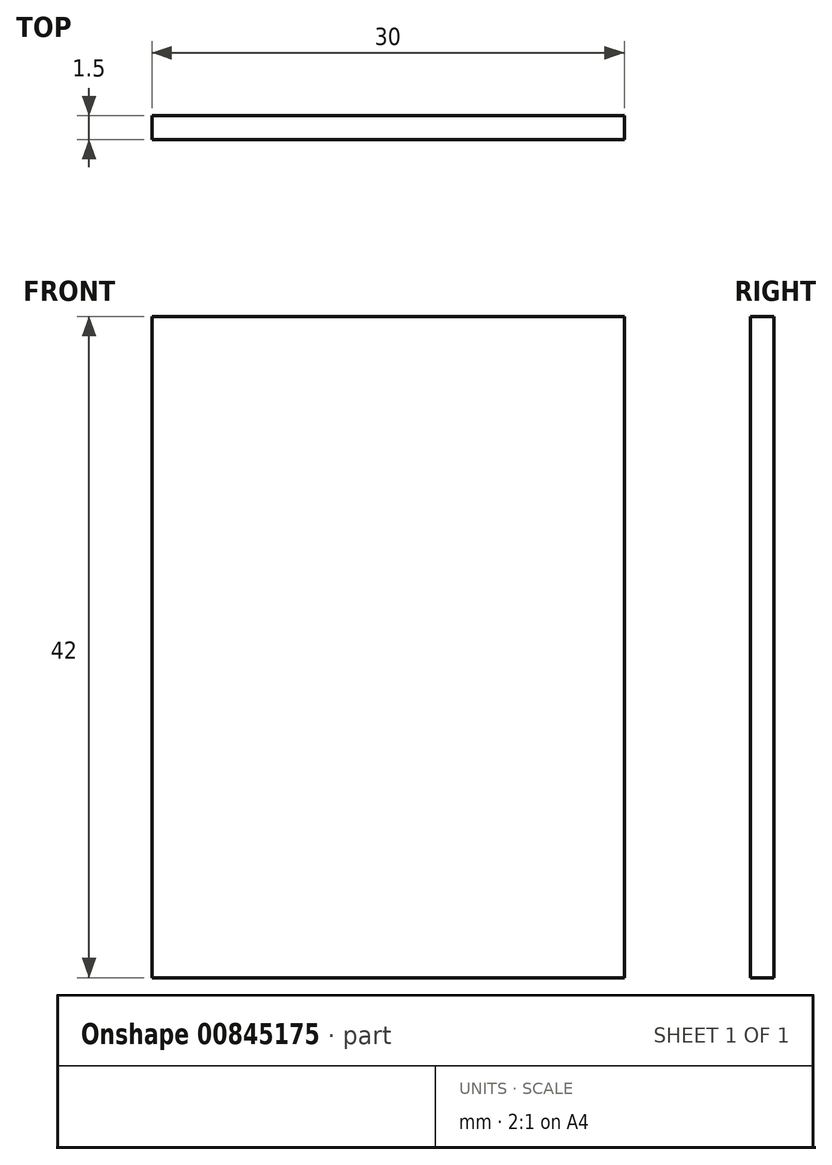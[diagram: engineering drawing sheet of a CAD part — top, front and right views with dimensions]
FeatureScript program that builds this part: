
annotation { "Feature Type Name" : "Feature", "Feature Type Description" : "" }
export const myFeature = defineFeature(function(context is Context, id is Id, definition is map)
    precondition{}
    {
        {
            var Q0;
            Q0=qCreatedBy(makeId("Front.planeOp"),FACE);
            var sketch = newSketch(context, id + "F0", { "sketchPlane" : qUnion([Q0])});
            skLineSegment(sketch, "E0.bottom", {"start": v(-15, -21) * mm, "end": v(15, -21) * mm});
            skLineSegment(sketch, "E0.top", {"start": v(-15, 21) * mm, "end": v(15, 21) * mm});
            skLineSegment(sketch, "E0.left", {"start": v(-15, -21) * mm, "end": v(-15, 21) * mm});
            skLineSegment(sketch, "E0.right", {"start": v(15, -21) * mm, "end": v(15, 21) * mm});
            skPoint(sketch, "E0.middle", {"position": v(0, 0) * mm});
            skSolve(sketch);
        }
        {
            var Q0;
            Q0=makeQuery(id+"F0.imprint","IMPRINT",FACE,{"disambiguationData":[TD([[makeQuery(id+"F0.imprint","IMPRINT",EDGE,{"derivedFrom":sQuery(id+"F0.wireOp",EDGE,"E0.bottom")}),1.0]])]});
            extrude(context, id + "F1", {"entities" : qUnion([Q0]), "depth" : 1.5 * mm, "offsetDistance" : 25 * mm});
        }
    });
